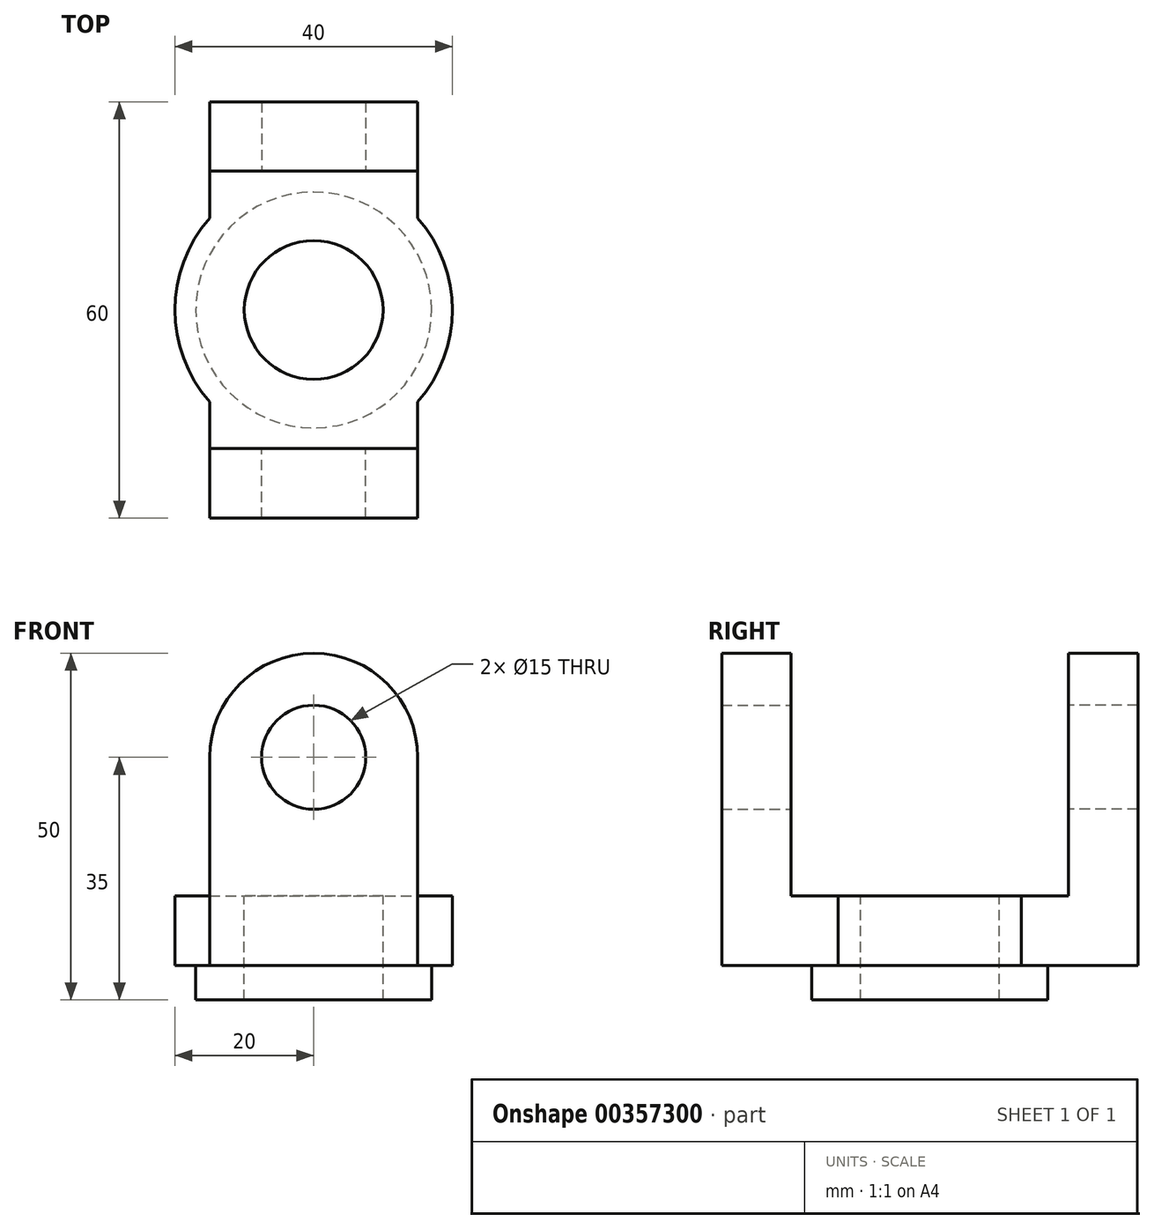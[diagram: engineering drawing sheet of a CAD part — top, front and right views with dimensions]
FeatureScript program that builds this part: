
annotation { "Feature Type Name" : "Feature", "Feature Type Description" : "" }
export const myFeature = defineFeature(function(context is Context, id is Id, definition is map)
    precondition{}
    {
        {
            var Q0;
            Q0=qCreatedBy(makeId("Front.planeOp"),FACE);
            var sketch = newSketch(context, id + "F0", { "sketchPlane" : qUnion([Q0])});
            skLineSegment(sketch, "E0.bottom", {"start": v(0, 0) * mm, "end": v(30, 0) * mm});
            skLineSegment(sketch, "E0.left", {"start": v(0, 0) * mm, "end": v(0, 30) * mm});
            skLineSegment(sketch, "E0.right", {"start": v(30, 0) * mm, "end": v(30, 30) * mm});
            skArc(sketch, "E1", {"start": v(30, 30) * mm, "mid": v(15, 45) * mm, "end": v(0, 30) * mm});
            skCircle(sketch, "E2", {"center": v(15, 30) * mm, "radius": 7.5 * mm});
            skSolve(sketch);
        }
        {
            var Q0;
            Q0 = qSketchRegion(id + "F0", true);
            extrude(context, id + "F1", {"entities" : qUnion([Q0]), "depth" : 10 * mm});
        }
        {
            var Q0;
            Q0=makeQuery(id+"F1.opExtrude","CAP_FACE",FACE,{"disambiguationData":[OSD([sQuery(id+"F0.wireOp",EDGE,"E0.bottom"),sQuery(id+"F0.wireOp",EDGE,"E0.left"),sQuery(id+"F0.wireOp",EDGE,"E0.right"),sQuery(id+"F0.wireOp",EDGE,"E1"),sQuery(id+"F0.wireOp",EDGE,"E2")])],"isStart":true});
            var sketch = newSketch(context, id + "F2", { "sketchPlane" : qUnion([Q0])});
            skLineSegment(sketch, "E3.bottom", {"start": v(0, 0) * mm, "end": v(-30, 0) * mm});
            skLineSegment(sketch, "E3.top", {"start": v(0, 10) * mm, "end": v(-30, 10) * mm});
            skLineSegment(sketch, "E3.left", {"start": v(0, 0) * mm, "end": v(0, 10) * mm});
            skLineSegment(sketch, "E3.right", {"start": v(-30, 0) * mm, "end": v(-30, 10) * mm});
            skSolve(sketch);
        }
        {
            var Q0;
            Q0 = qSketchRegion(id + "F2", true);
            extrude(context, id + "F3", {"entities" : qUnion([Q0]), "operationType" : NewBodyOperationType.ADD, "depth" : 5 * mm});
        }
        {
            var Q0;
            Q0=makeQuery(id+"F3.opExtrude","CAP_FACE",FACE,{"disambiguationData":[OSD([sQuery(id+"F2.wireOp",EDGE,"E3.bottom"),sQuery(id+"F2.wireOp",EDGE,"E3.top"),sQuery(id+"F2.wireOp",EDGE,"E3.left"),sQuery(id+"F2.wireOp",EDGE,"E3.right")])],"isStart":false});
            cPlane(context, id + "F4", {"entities" : qUnion([Q0]), "cplaneType" : CPlaneType.OFFSET, "offset" : 15 * mm, "width" : 150 * mm, "height" : 150 * mm});
        }
        {
            var Q0;
            Q0=makeQuery(id+"F1.opExtrude","SWEPT_BODY",BODY,{"disambiguationData":[OSD([sQuery(id+"F0.wireOp",EDGE,"E0.bottom"),sQuery(id+"F0.wireOp",EDGE,"E0.left"),sQuery(id+"F0.wireOp",EDGE,"E0.right"),sQuery(id+"F0.wireOp",EDGE,"E1"),sQuery(id+"F0.wireOp",EDGE,"E2")])]});
            var Q1;
            Q1=qCreatedBy(id+"F4.planeOp",FACE);
            mirror(context, id + "F5", {"entities" : qUnion([Q0]), "mirrorPlane" : qUnion([Q1])});
        }
        {
            var Q0;
            Q0=makeQuery(id+"F5.opPattern","COPY",FACE,{"derivedFrom":makeQuery(id+"F3.opExtrude","CAP_FACE",FACE,{"disambiguationData":[OSD([sQuery(id+"F2.wireOp",EDGE,"E3.bottom"),sQuery(id+"F2.wireOp",EDGE,"E3.top"),sQuery(id+"F2.wireOp",EDGE,"E3.left"),sQuery(id+"F2.wireOp",EDGE,"E3.right")])],"isStart":false}),"instanceName":"1"});
            var Q1;
            Q1=makeQuery(id+"F3.opExtrude","CAP_FACE",FACE,{"disambiguationData":[OSD([sQuery(id+"F2.wireOp",EDGE,"E3.bottom"),sQuery(id+"F2.wireOp",EDGE,"E3.top"),sQuery(id+"F2.wireOp",EDGE,"E3.left"),sQuery(id+"F2.wireOp",EDGE,"E3.right")])],"isStart":false});
            extrude(context, id + "F6", {"entities" : qUnion([Q0]), "operationType" : NewBodyOperationType.ADD, "endBound" : BoundingType.UP_TO_SURFACE, "endBoundEntityFace" : qUnion([Q1]), "depth" : 25 * mm});
        }
        {
            var Q0;
            {var subQ0=sQuery(id+"F2.wireOp",EDGE,"E3.top");var subQ1=makeQuery(id+"F3.opExtrude","SWEPT_FACE",FACE,{"disambiguationData":[OSD([subQ0])]});Q0=makeQuery(id+"F6.boolean.opBoolean","MERGE",FACE,{"derivedFrom":[subQ1,makeQuery(id+"F5.opPattern","COPY",FACE,{"derivedFrom":subQ1,"instanceName":"1"}),makeQuery(id+"F6.opExtrude","SWEPT_FACE",FACE,{"disambiguationData":[OSD([subQ0])]})]});}
            var sketch = newSketch(context, id + "F7", { "sketchPlane" : qUnion([Q0])});
            skCircle(sketch, "E4", {"center": v(15, 20) * mm, "radius": 10 * mm});
            skPoint(sketch, "E4.centerSnap0", {"position": v(15, 40) * mm});
            skPoint(sketch, "E4.centerSnap1", {"position": v(0, 20) * mm});
            skSolve(sketch);
        }
        {
            var Q0;
            Q0 = qSketchRegion(id + "F7", true);
            var Q1;
            {var subQ0=sQuery(id+"F2.wireOp",EDGE,"E3.bottom");var subQ1=makeQuery(id+"F3.boolean.opBoolean","MERGE",FACE,{"derivedFrom":[makeQuery(id+"F1.opExtrude","SWEPT_FACE",FACE,{"disambiguationData":[OSD([sQuery(id+"F0.wireOp",EDGE,"E0.bottom")])]}),makeQuery(id+"F3.opExtrude","SWEPT_FACE",FACE,{"disambiguationData":[OSD([subQ0])]})]});Q1=makeQuery(id+"F6.boolean.opBoolean","MERGE",FACE,{"derivedFrom":[subQ1,makeQuery(id+"F5.opPattern","COPY",FACE,{"derivedFrom":subQ1,"instanceName":"1"}),makeQuery(id+"F6.opExtrude","SWEPT_FACE",FACE,{"disambiguationData":[OSD([subQ0])]})]});}
            extrude(context, id + "F8", {"entities" : qUnion([Q0]), "operationType" : NewBodyOperationType.REMOVE, "endBound" : BoundingType.UP_TO_SURFACE, "oppositeDirection" : true, "endBoundEntityFace" : qUnion([Q1]), "depth" : 25 * mm});
        }
        {
            var Q0;
            {var subQ0=sQuery(id+"F2.wireOp",EDGE,"E3.top");var subQ1=makeQuery(id+"F3.opExtrude","SWEPT_FACE",FACE,{"disambiguationData":[OSD([subQ0])]});Q0=makeQuery(id+"F6.boolean.opBoolean","MERGE",FACE,{"derivedFrom":[subQ1,makeQuery(id+"F5.opPattern","COPY",FACE,{"derivedFrom":subQ1,"instanceName":"1"}),makeQuery(id+"F6.opExtrude","SWEPT_FACE",FACE,{"disambiguationData":[OSD([subQ0])]})]});}
            var sketch = newSketch(context, id + "F9", { "sketchPlane" : qUnion([Q0])});
            skArc(sketch, "E5", {"start": v(0, 33.23) * mm, "mid": v(-5, 20) * mm, "end": v(0, 6.77) * mm});
            skLineSegment(sketch, "E6", {"start": v(0, 33.23) * mm, "end": v(0, 6.77) * mm});
            skLineSegment(sketch, "E7", {"start": v(30, 33.23) * mm, "end": v(30, 6.77) * mm});
            skArc(sketch, "E8.trimOffspring", {"start": v(30, 6.77) * mm, "mid": v(35, 20) * mm, "end": v(30, 33.23) * mm});
            skSolve(sketch);
        }
        {
            var Q0;
            Q0 = qSketchRegion(id + "F9", true);
            extrude(context, id + "F10", {"entities" : qUnion([Q0]), "operationType" : NewBodyOperationType.ADD, "oppositeDirection" : true, "depth" : 10 * mm});
        }
        {
            var Q0;
            {var subQ0=sQuery(id+"F2.wireOp",EDGE,"E3.bottom");var subQ1=makeQuery(id+"F3.boolean.opBoolean","MERGE",FACE,{"derivedFrom":[makeQuery(id+"F1.opExtrude","SWEPT_FACE",FACE,{"disambiguationData":[OSD([sQuery(id+"F0.wireOp",EDGE,"E0.bottom")])]}),makeQuery(id+"F3.opExtrude","SWEPT_FACE",FACE,{"disambiguationData":[OSD([subQ0])]})]});Q0=makeQuery(id+"F10.boolean.opBoolean","MERGE",FACE,{"derivedFrom":[makeQuery(id+"F6.boolean.opBoolean","MERGE",FACE,{"derivedFrom":[subQ1,makeQuery(id+"F5.opPattern","COPY",FACE,{"derivedFrom":subQ1,"instanceName":"1"}),makeQuery(id+"F6.opExtrude","SWEPT_FACE",FACE,{"disambiguationData":[OSD([subQ0])]})]}),makeQuery(id+"F10.opExtrude","CAP_FACE",FACE,{"disambiguationData":[OSD([sQuery(id+"F9.wireOp",EDGE,"E5"),sQuery(id+"F9.wireOp",EDGE,"E6")])],"isStart":false}),makeQuery(id+"F10.opExtrude","CAP_FACE",FACE,{"disambiguationData":[OSD([sQuery(id+"F9.wireOp",EDGE,"E7"),sQuery(id+"F9.wireOp",EDGE,"E8.trimOffspring")])],"isStart":false})]});}
            var sketch = newSketch(context, id + "F11", { "sketchPlane" : qUnion([Q0])});
            skCircle(sketch, "E9", {"center": v(15, -20) * mm, "radius": 17 * mm});
            skSolve(sketch);
        }
        {
            var Q0;
            Q0 = qSketchRegion(id + "F11", true);
            extrude(context, id + "F12", {"entities" : qUnion([Q0]), "operationType" : NewBodyOperationType.ADD, "depth" : 5 * mm});
        }
        {
            var Q0;
            Q0=makeQuery(id+"F12.opExtrude","CAP_FACE",FACE,{"disambiguationData":[OSD([sQuery(id+"F11.wireOp",EDGE,"E9")])],"isStart":true});
            var Q1;
            Q1=makeQuery(id+"F12.opExtrude","CAP_FACE",FACE,{"disambiguationData":[OSD([sQuery(id+"F11.wireOp",EDGE,"E9")])],"isStart":false});
            extrude(context, id + "F13", {"entities" : qUnion([Q0]), "operationType" : NewBodyOperationType.REMOVE, "endBound" : BoundingType.UP_TO_SURFACE, "oppositeDirection" : true, "endBoundEntityFace" : qUnion([Q1]), "depth" : 25 * mm});
        }
    });
